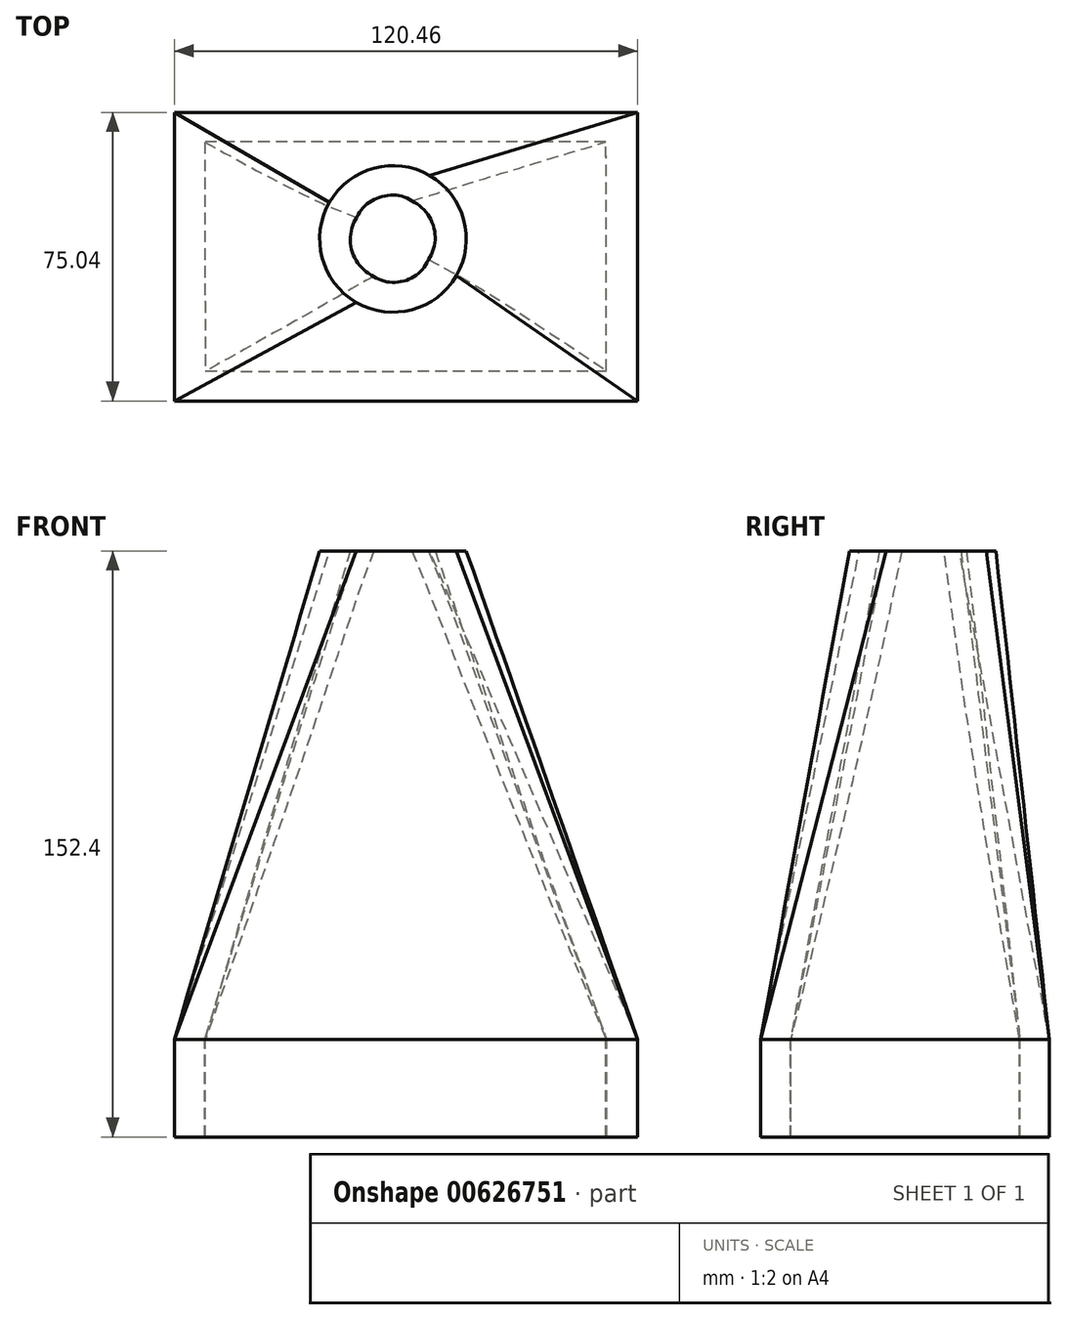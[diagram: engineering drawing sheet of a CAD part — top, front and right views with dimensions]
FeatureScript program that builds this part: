
annotation { "Feature Type Name" : "Feature", "Feature Type Description" : "" }
export const myFeature = defineFeature(function(context is Context, id is Id, definition is map)
    precondition{}
    {
        {
            var Q0;
            Q0=qCreatedBy(makeId("Top.planeOp"),FACE);
            var sketch = newSketch(context, id + "F0", { "sketchPlane" : qUnion([Q0])});
            skLineSegment(sketch, "E0.bottom", {"start": v(-56.86, 32.9) * mm, "end": v(63.6, 32.9) * mm});
            skLineSegment(sketch, "E0.top", {"start": v(-56.86, -42.13) * mm, "end": v(63.6, -42.13) * mm});
            skLineSegment(sketch, "E0.left", {"start": v(-56.86, 32.9) * mm, "end": v(-56.86, -42.13) * mm});
            skLineSegment(sketch, "E0.right", {"start": v(63.6, 32.9) * mm, "end": v(63.6, -42.13) * mm});
            skSolve(sketch);
        }
        {
            var Q0;
            Q0=qCreatedBy(makeId("Top.planeOp"),FACE);
            cPlane(context, id + "F1", {"entities" : qUnion([Q0]), "cplaneType" : CPlaneType.OFFSET, "offset" : 127 * mm, "width" : 152.4 * mm, "height" : 152.4 * mm});
        }
        {
            var Q0;
            Q0=qCreatedBy(id+"F1.planeOp",FACE);
            var sketch = newSketch(context, id + "F2", { "sketchPlane" : qUnion([Q0])});
            skCircle(sketch, "E1", {"center": v(0, 0) * mm, "radius": 19.05 * mm});
            skSolve(sketch);
        }
        {
            var Q0;
            Q0=makeQuery(id+"F0.imprint","IMPRINT",FACE,{"disambiguationData":[TD([[makeQuery(id+"F0.imprint","IMPRINT",EDGE,{"derivedFrom":sQuery(id+"F0.wireOp",EDGE,"E0.bottom")}),-1.0]])]});
            var Q1;
            Q1=makeQuery(id+"F2.imprint","IMPRINT",FACE,{"disambiguationData":[TD([[makeQuery(id+"F2.imprint","IMPRINT",EDGE,{"derivedFrom":sQuery(id+"F2.wireOp",EDGE,"E1")}),1.0]])]});
            loft(context, id + "F3", {"sheetProfilesArray" : [{ "sheetProfileEntities" : qUnion([Q0]) }, { "sheetProfileEntities" : qUnion([Q1]) }]});
        }
        {
            var Q0;
            Q0=makeQuery(id+"F3.opLoft","CAP_FACE",FACE,{"disambiguationData":[OSD([makeQuery(id+"F0.imprint","IMPRINT",FACE,{"disambiguationData":[TD([[makeQuery(id+"F0.imprint","IMPRINT",EDGE,{"derivedFrom":sQuery(id+"F0.wireOp",EDGE,"E0.bottom")}),-1.0]])]})])],"isStart":true});
            var Q1;
            Q1=makeQuery(id+"F3.opLoft","CAP_FACE",FACE,{"disambiguationData":[OSD([makeQuery(id+"F2.imprint","IMPRINT",FACE,{"disambiguationData":[TD([[makeQuery(id+"F2.imprint","IMPRINT",EDGE,{"derivedFrom":sQuery(id+"F2.wireOp",EDGE,"E1")}),1.0]])]})])],"isStart":true});
            shell(context, id + "F4", {"entities" : qUnion([Q0, Q1]), "thickness" : 7.62 * mm});
        }
        {
            var Q0;
            Q0=makeQuery(id+"F3.opLoft","CAP_FACE",FACE,{"disambiguationData":[OSD([makeQuery(id+"F0.imprint","IMPRINT",FACE,{"disambiguationData":[TD([[makeQuery(id+"F0.imprint","IMPRINT",EDGE,{"derivedFrom":sQuery(id+"F0.wireOp",EDGE,"E0.bottom")}),-1.0]])]})])],"isStart":true});
            extrude(context, id + "F5", {"entities" : qUnion([Q0]), "operationType" : NewBodyOperationType.ADD, "depth" : 25.4 * mm, "offsetDistance" : 25.4 * mm});
        }
    });
